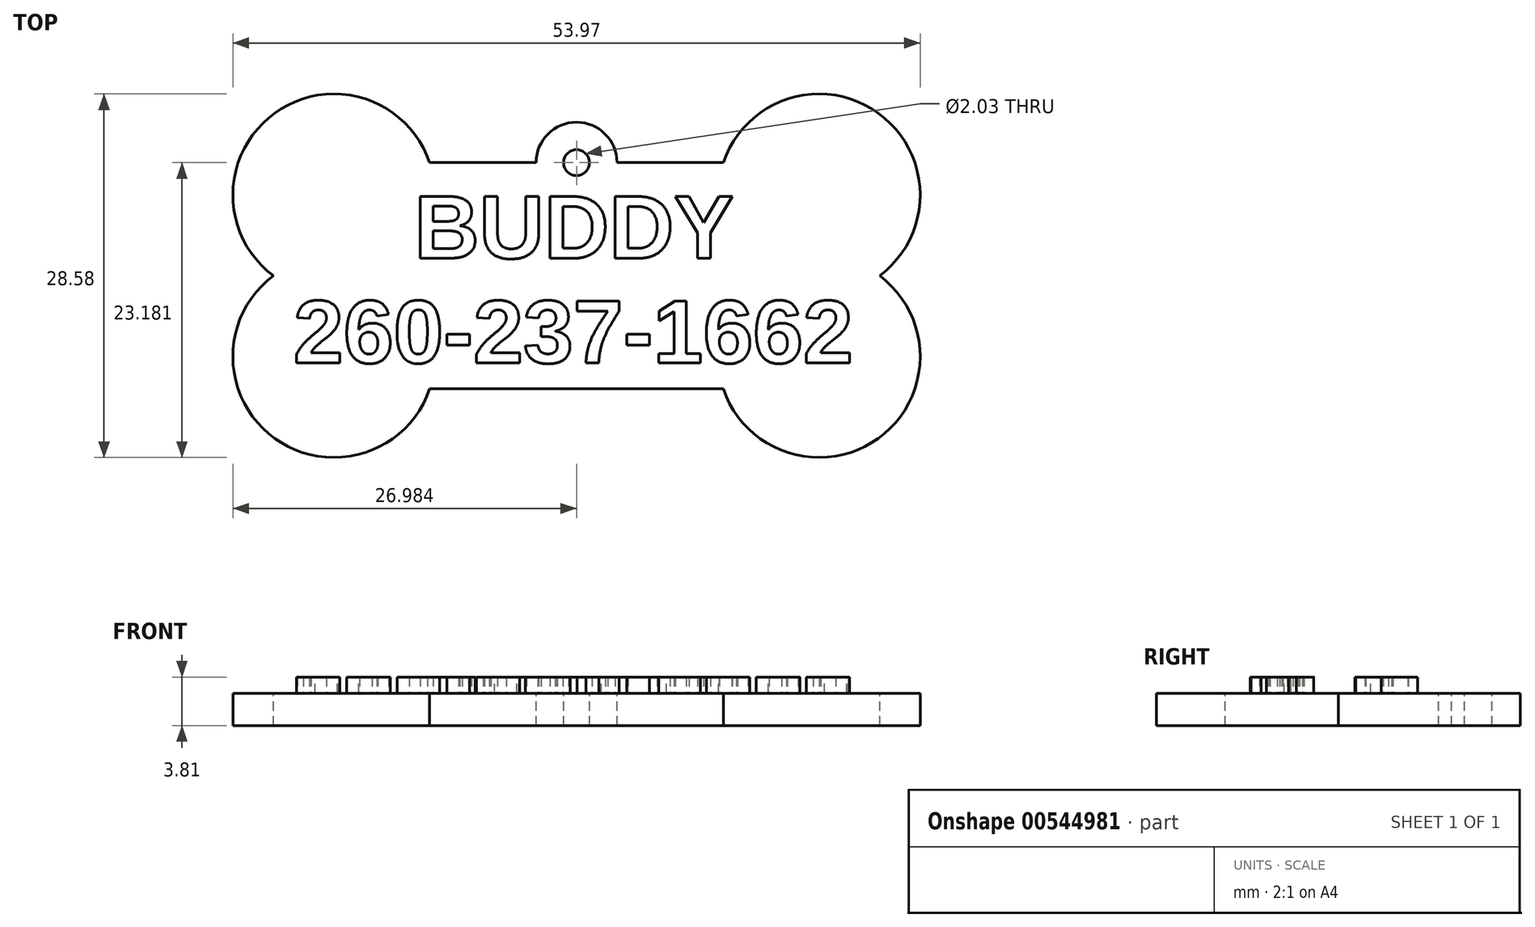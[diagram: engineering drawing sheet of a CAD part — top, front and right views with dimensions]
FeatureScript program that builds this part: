
annotation { "Feature Type Name" : "Feature", "Feature Type Description" : "" }
export const myFeature = defineFeature(function(context is Context, id is Id, definition is map)
    precondition{}
    {
        {
            var Q0;
            Q0=qCreatedBy(makeId("Top.planeOp"),FACE);
            var sketch = newSketch(context, id + "F0", { "sketchPlane" : qUnion([Q0])});
            skArc(sketch, "E0", {"start": v(-23.64, 27.3) * mm, "mid": v(-35.81, 31.18) * mm, "end": v(-35.92, 18.4) * mm});
            skArc(sketch, "E1", {"start": v(11.7, 18.4) * mm, "mid": v(11.6, 31.18) * mm, "end": v(-0.58, 27.3) * mm});
            skArc(sketch, "E2", {"start": v(-35.92, 18.4) * mm, "mid": v(-35.81, 5.62) * mm, "end": v(-23.64, 9.51) * mm});
            skArc(sketch, "E3", {"start": v(-0.58, 9.51) * mm, "mid": v(11.6, 5.62) * mm, "end": v(11.7, 18.4) * mm});
            skArc(sketch, "E4", {"start": v(-8.93, 27.3) * mm, "mid": v(-12.1, 30.47) * mm, "end": v(-15.28, 27.3) * mm});
            skLineSegment(sketch, "E5", {"start": v(-23.64, 27.3) * mm, "end": v(-15.28, 27.3) * mm});
            skLineSegment(sketch, "E6.0", {"start": v(-23.64, 9.51) * mm, "end": v(-0.58, 9.51) * mm});
            skPoint(sketch, "E7.orphan", {"position": v(-31.16, 27.3) * mm});
            skPoint(sketch, "E8.orphan", {"position": v(6.94, 27.3) * mm});
            skLineSegment(sketch, "E9.trimOffspring", {"start": v(-8.93, 27.3) * mm, "end": v(-0.58, 27.3) * mm});
            skCircle(sketch, "E10", {"center": v(-12.1, 27.3) * mm, "radius": 1.02 * mm});
            skSolve(sketch);
        }
        {
            var Q0;
            Q0=qSketchRegion(id+"F0",true);
            extrude(context, id + "F1", {"entities" : qUnion([Q0]), "oppositeDirection" : true, "depth" : 2.54 * mm, "offsetDistance" : 25.4 * mm});
        }
        {
            var Q0;
            Q0=makeQuery(id+"F1.opExtrude","CAP_FACE",FACE,{"disambiguationData":[OSD([sQuery(id+"F0.wireOp",EDGE,"E0"),sQuery(id+"F0.wireOp",EDGE,"E1"),sQuery(id+"F0.wireOp",EDGE,"E2"),sQuery(id+"F0.wireOp",EDGE,"E3"),sQuery(id+"F0.wireOp",EDGE,"E4"),sQuery(id+"F0.wireOp",EDGE,"E5"),sQuery(id+"F0.wireOp",EDGE,"E6.0"),sQuery(id+"F0.wireOp",EDGE,"E9.trimOffspring"),sQuery(id+"F0.wireOp",EDGE,"E10")])],"isStart":true});
            var sketch = newSketch(context, id + "F2", { "sketchPlane" : qUnion([Q0])});
            skText(sketch, "E11", { "text": "BUDDY", "fontName": "Arimo-Bold.ttf"});
            const initialGuessF2  = {"E11": [-0.02484, 0.01978, 1, 0, 0.00508]};
            skSetInitialGuess(sketch, initialGuessF2);
            skSolve(sketch);
        }
        {
            var Q0;
            Q0=qSketchRegion(id+"F2",true);
            extrude(context, id + "F3", {"entities" : qUnion([Q0]), "operationType" : NewBodyOperationType.ADD, "depth" : 1.27 * mm, "offsetDistance" : 25.4 * mm});
        }
        {
            var Q0;
            {var subQ0=sQuery(id+"F0.wireOp",EDGE,"E6.0");var subQ1=sQuery(id+"F0.wireOp",EDGE,"E5");var subQ2=sQuery(id+"F0.wireOp",EDGE,"E0");var subQ3=sQuery(id+"F0.wireOp",EDGE,"E4");var subQ4=sQuery(id+"F0.wireOp",EDGE,"E3");var subQ5=sQuery(id+"F0.wireOp",EDGE,"E1");var subQ6=sQuery(id+"F0.wireOp",EDGE,"E2");var subQ7=sQuery(id+"F0.wireOp",EDGE,"E9.trimOffspring");var subQ8=sQuery(id+"F0.wireOp",EDGE,"E10");Q0=makeQuery(id+"F3.boolean.opBoolean","SPLIT",FACE,{"disambiguationData":[TD([makeQuery(id+"F1.opExtrude","SWEPT_FACE",FACE,{"disambiguationData":[OSD([subQ2])]})])],"derivedFrom":makeQuery(id+"F1.opExtrude","CAP_FACE",FACE,{"disambiguationData":[OSD([subQ2,subQ5,subQ6,subQ4,subQ3,subQ1,subQ0,subQ7,subQ8])],"isStart":true})});}
            var sketch = newSketch(context, id + "F4", { "sketchPlane" : qUnion([Q0])});
            skText(sketch, "E12", { "text": "260-237-1662", "fontName": "Arimo-Bold.ttf"});
            const initialGuessF4  = {"E12": [-0.03433, 0.01155, 1, 0, 0.00508]};
            skSetInitialGuess(sketch, initialGuessF4);
            skSolve(sketch);
        }
        {
            var Q0;
            Q0=qSketchRegion(id+"F4",true);
            extrude(context, id + "F5", {"entities" : qUnion([Q0]), "operationType" : NewBodyOperationType.ADD, "depth" : 1.27 * mm, "offsetDistance" : 25.4 * mm});
        }
    });
